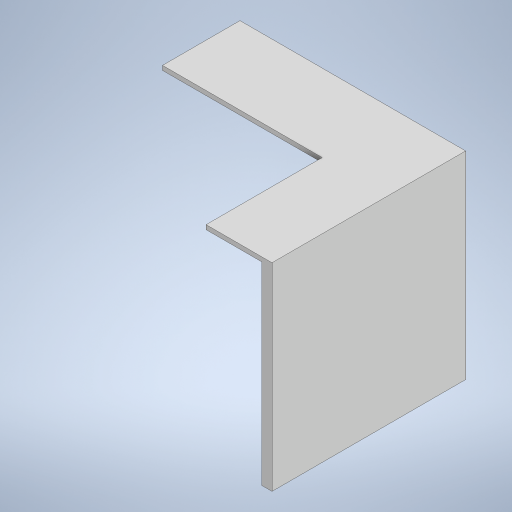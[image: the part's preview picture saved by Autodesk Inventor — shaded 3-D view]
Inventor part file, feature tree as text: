
AUTODESK INVENTOR PART (.ipt)
format: ipt  version: 2024 (Build 280153000, 153)  size: 324,096 bytes
history: native  units: mm
features: extrude x11, sketch x11
ambient origin geometry x8: Origin, YZ Plane, XZ Plane, XY Plane, X Axis, Y Axis, Z Axis, Center Point
bodies: Solid1 (feature_tree)
feature tree (22):
  extrude  "Top"  Depth=160.0mm
  extrude  "Right"  Depth=179.5mm
  extrude  "Left"  Depth=215.9mm
  extrude  "Plexiglass Cut"  Depth=25.4mm
  extrude  "Bottom"  Depth=50.8mm TaperAngle=0.0deg
  extrude  "Top Flattening"  Depth=50.8mm TaperAngle=0.0deg
  extrude  "Outer Side Flattening"  Depth=12.7mm TaperAngle=0.0deg
  extrude  "Bottom Flattening"  Depth=22.4mm TaperAngle=0.0deg
  extrude  "Inner Flattening"  Depth=22.389425mm
  extrude  "Bottom Cut"  Depth=22.4mm TaperAngle=0.0deg
  extrude  "Quarter Cut"  Depth=22.4mm TaperAngle=0.0deg
  sketch  "Sketch1"  dims[d11=220.0mm d12=160.0mm]
  sketch  "Sketch3"  dims[d15=248.6mm d16=179.5mm]
  sketch  "Sketch4"  dims[d18=304.8mm d19=215.9mm]
  sketch  "Sketch5"  dims[d20=25.4mm d21=0.0mm d22=25.4mm]
  sketch  "Sketch6"  dims[d25=266.7mm d26=50.8mm d27=0.0mm]
  sketch  "Sketch9"  dims[d28=266.7mm d29=50.8mm d30=0.0mm]
  sketch  "Sketch10"  dims[d31=12.7mm d32=304.8mm d33=0.0mm]
  sketch  "Sketch11"  dims[d34=25.4mm d35=0.0mm d46=22.4mm d47=0.0mm]
  sketch  "Sketch12"  dims[d48=22.389425mm d49=22.389425mm]
  sketch  "Sketch13"  dims[d50=0.0mm d51=0.0mm d52=22.4mm d53=0.0mm]
  sketch  "Sketch14"  dims[d54=296.8mm d55=22.4mm d56=0.0mm d57=0.0mm d58=0.0mm d59=0.0mm d60=0.0mm]
